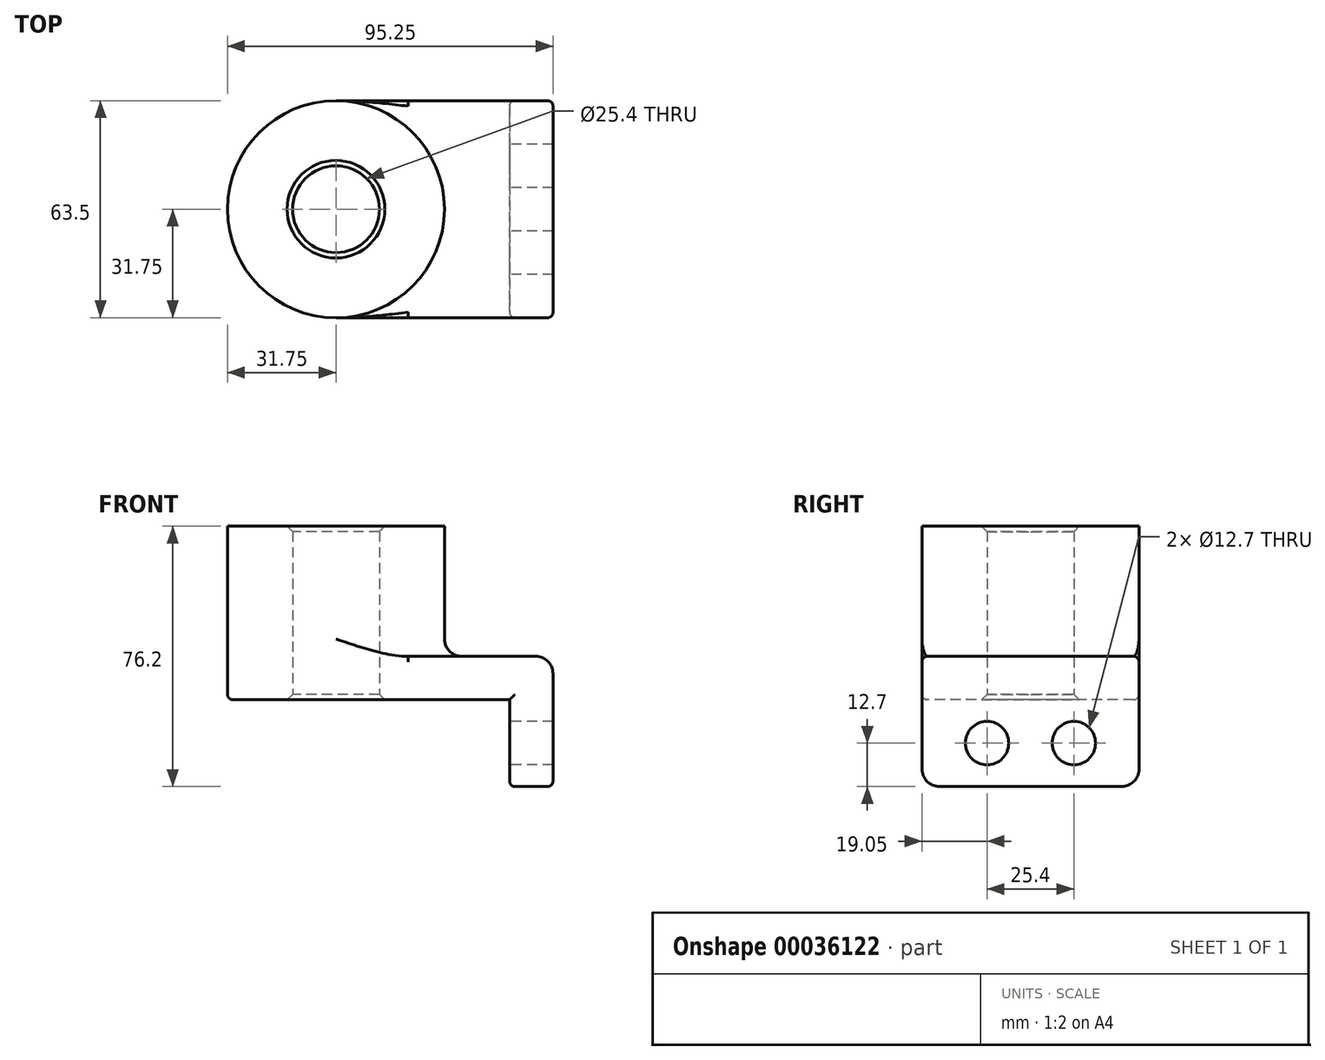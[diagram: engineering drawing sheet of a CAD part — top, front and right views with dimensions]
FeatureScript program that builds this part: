
annotation { "Feature Type Name" : "Feature", "Feature Type Description" : "" }
export const myFeature = defineFeature(function(context is Context, id is Id, definition is map)
    precondition{}
    {
        {
            var Q0;
            Q0=qCreatedBy(makeId("Top.planeOp"),FACE);
            var sketch = newSketch(context, id + "F0", { "sketchPlane" : qUnion([Q0])});
            skLineSegment(sketch, "E0.rect.bottom", {"start": v(25.4, 31.75) * mm, "end": v(-25.4, 31.75) * mm});
            skLineSegment(sketch, "E0.rect.top", {"start": v(25.4, -31.75) * mm, "end": v(-25.4, -31.75) * mm});
            skLineSegment(sketch, "E0.rect.left", {"start": v(25.4, 31.75) * mm, "end": v(25.4, -31.75) * mm});
            skLineSegment(sketch, "E0.rect.right", {"start": v(-25.4, 31.75) * mm, "end": v(-25.4, -31.75) * mm});
            skPoint(sketch, "E0.rect.middle", {"position": v(0, 0) * mm});
            skCircle(sketch, "E1", {"center": v(-25.4, 0) * mm, "radius": 12.7 * mm});
            skCircle(sketch, "E2", {"center": v(-25.4, 0) * mm, "radius": 31.75 * mm});
            skSolve(sketch);
        }
        {
            var Q0;
            Q0 = qSketchRegion(id + "F0", true);
            extrude(context, id + "F1", {"entities" : qUnion([Q0]), "depth" : 12.7 * mm});
        }
        {
            var Q0;
            {var subQ1=sQuery(id+"F0.wireOp",EDGE,"E0.rect.right");var subQ4=sQuery(id+"F0.wireOp",EDGE,"E1");var subQ6=makeQuery(id+"F0.imprint","INTERSECT",VERTEX,{"disambiguationData":[OD(0.0)],"derivedFrom":[subQ1,subQ4]});Q0=makeQuery(id+"F0.imprint","IMPRINT",FACE,{"disambiguationData":[TD([[makeQuery(id+"F0.imprint","IMPRINT",EDGE,{"disambiguationData":[TD([[subQ6,-1.0]])],"derivedFrom":subQ4}),-1.0]])]});}
            var Q1;
            {var subQ1=sQuery(id+"F0.wireOp",EDGE,"E0.rect.right");var subQ4=sQuery(id+"F0.wireOp",EDGE,"E1");var subQ6=makeQuery(id+"F0.imprint","INTERSECT",VERTEX,{"disambiguationData":[OD(0.0)],"derivedFrom":[subQ1,subQ4]});Q1=makeQuery(id+"F0.imprint","IMPRINT",FACE,{"disambiguationData":[TD([[makeQuery(id+"F0.imprint","IMPRINT",EDGE,{"disambiguationData":[TD([[subQ6,1.0]])],"derivedFrom":subQ4}),-1.0]])]});}
            extrude(context, id + "F2", {"entities" : qUnion([Q0, Q1]), "operationType" : NewBodyOperationType.ADD, "depth" : 50.8 * mm});
        }
        {
            var Q0;
            Q0=makeQuery(id+"F1.opExtrude","SWEPT_FACE",FACE,{"disambiguationData":[OSD([sQuery(id+"F0.wireOp",EDGE,"E0.rect.left")])]});
            var sketch = newSketch(context, id + "F3", { "sketchPlane" : qUnion([Q0])});
            skLineSegment(sketch, "E3.bottom", {"start": v(-31.75, 12.7) * mm, "end": v(31.75, 12.7) * mm});
            skLineSegment(sketch, "E3.top", {"start": v(-31.75, -25.4) * mm, "end": v(31.75, -25.4) * mm});
            skLineSegment(sketch, "E3.left", {"start": v(-31.75, 12.7) * mm, "end": v(-31.75, -25.4) * mm});
            skLineSegment(sketch, "E3.right", {"start": v(31.75, 12.7) * mm, "end": v(31.75, -25.4) * mm});
            skCircle(sketch, "E4", {"center": v(-12.7, -12.7) * mm, "radius": 6.35 * mm});
            skLineSegment(sketch, "E5", {"start": v(0, 0) * mm, "end": v(0, -25.4) * mm, "construction": true});
            skCircle(sketch, "E6.MirrorC", {"center": v(12.7, -12.7) * mm, "radius": 6.35 * mm});
            skCircle(sketch, "E7.MirrorC", {"center": v(-12.7, -12.7) * mm, "radius": 6.35 * mm, "construction": true});
            skSolve(sketch);
        }
        {
            var Q0;
            Q0 = qSketchRegion(id + "F3", true);
            extrude(context, id + "F4", {"entities" : qUnion([Q0]), "operationType" : NewBodyOperationType.ADD, "depth" : 12.7 * mm});
        }
        {
            var Q0;
            {var subQ0=sQuery(id+"F0.wireOp",EDGE,"E2");Q0=makeQuery(id+"F2.boolean.opBoolean","INTERSECT",EDGE,{"derivedFrom":[makeQuery(id+"F1.opExtrude","CAP_FACE",FACE,{"disambiguationData":[OSD([sQuery(id+"F0.wireOp",EDGE,"E0.rect.bottom"),sQuery(id+"F0.wireOp",EDGE,"E0.rect.top"),sQuery(id+"F0.wireOp",EDGE,"E0.rect.left"),sQuery(id+"F0.wireOp",EDGE,"E1"),subQ0])],"isStart":false}),makeQuery(id+"F2.opExtrude","SWEPT_FACE",FACE,{"disambiguationData":[OSD([subQ0])]})]});}
            var Q1;
            Q1=makeQuery(id+"F4.opExtrude","CAP_EDGE",EDGE,{"disambiguationData":[OSD([sQuery(id+"F3.wireOp",EDGE,"E3.bottom")])],"isStart":false});
            var Q2;
            Q2=makeQuery(id+"F4.opExtrude","SWEPT_EDGE",EDGE,{"disambiguationData":[OSD([sQuery(id+"F3.wireOp",EDGE,"E3.top"),sQuery(id+"F3.wireOp",EDGE,"E3.left")])]});
            var Q3;
            Q3=makeQuery(id+"F4.opExtrude","SWEPT_EDGE",EDGE,{"disambiguationData":[OSD([sQuery(id+"F3.wireOp",EDGE,"E3.top"),sQuery(id+"F3.wireOp",EDGE,"E3.right")])]});
            fillet(context, id + "F5", {"entities" : qUnion([Q0, Q1, Q2, Q3]), "radius" : 5.08 * mm, "tangentPropagation" : true, "allowEdgeOverflow" : false});
        }
        {
            var Q0;
            Q0=makeQuery(id+"F4.boolean.opBoolean","MERGE",EDGE,{"derivedFrom":[makeQuery(id+"F1.opExtrude","CAP_EDGE",EDGE,{"disambiguationData":[OSD([sQuery(id+"F0.wireOp",EDGE,"E0.rect.top")])],"isStart":false}),makeQuery(id+"F4.opExtrude","SWEPT_EDGE",EDGE,{"disambiguationData":[OSD([sQuery(id+"F3.wireOp",EDGE,"E3.bottom"),sQuery(id+"F3.wireOp",EDGE,"E3.left")])]})]});
            var Q1;
            Q1=makeQuery(id+"F1.opExtrude","CAP_EDGE",EDGE,{"disambiguationData":[OSD([sQuery(id+"F0.wireOp",EDGE,"E0.rect.top")])],"isStart":true});
            var Q2;
            Q2=makeQuery(id+"F4.opExtrude","CAP_EDGE",EDGE,{"disambiguationData":[OSD([sQuery(id+"F3.wireOp",EDGE,"E3.left")])],"isStart":true});
            fillet(context, id + "F6", {"entities" : qUnion([Q0, Q1, Q2]), "radius" : 1.59 * mm, "tangentPropagation" : true, "allowEdgeOverflow" : false});
        }
        {
            var Q0;
            {var subQ0=sQuery(id+"F0.wireOp",EDGE,"E1");Q0=makeQuery(id+"F2.boolean.opBoolean","MERGE",FACE,{"derivedFrom":[makeQuery(id+"F1.opExtrude","SWEPT_FACE",FACE,{"disambiguationData":[OSD([subQ0])]}),makeQuery(id+"F2.opExtrude","SWEPT_FACE",FACE,{"disambiguationData":[OSD([subQ0])]})]});}
            chamfer(context, id + "F7", {"entities" : qUnion([Q0]), "width" : 1.59 * mm, "tangentPropagation" : true});
        }
    });
